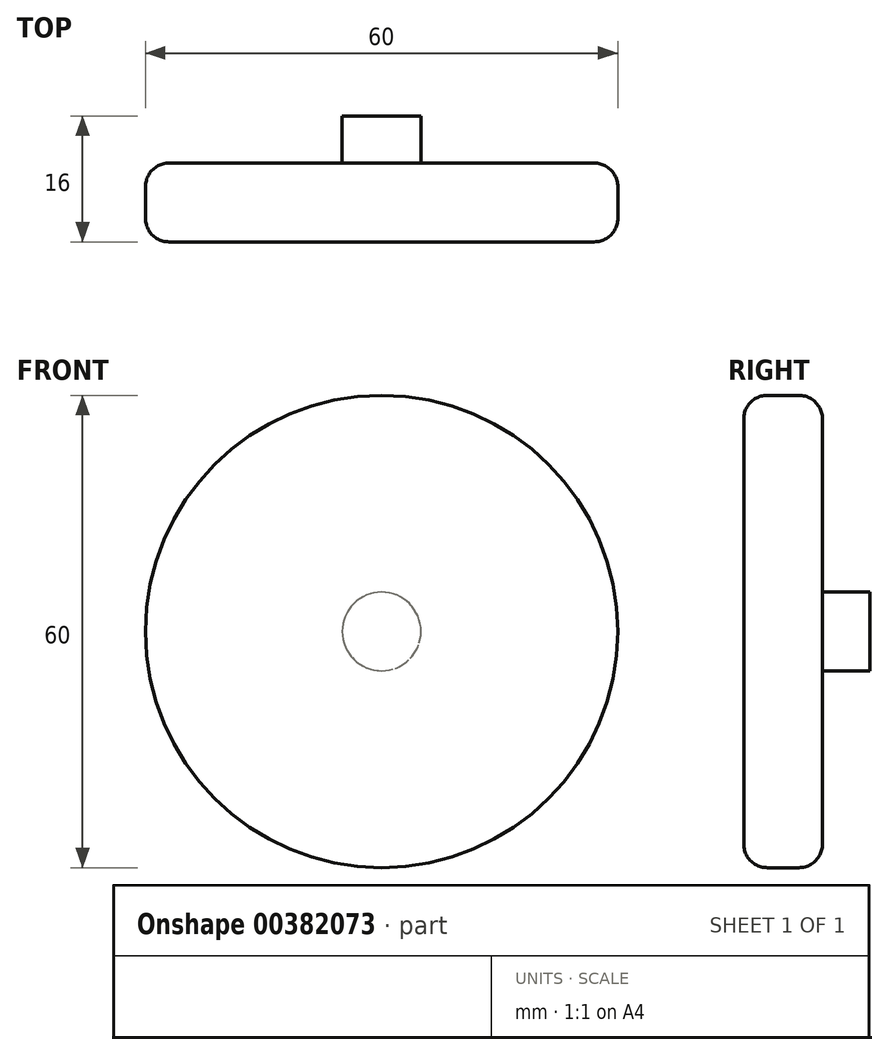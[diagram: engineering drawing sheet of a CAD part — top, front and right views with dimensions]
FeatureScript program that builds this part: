
annotation { "Feature Type Name" : "Feature", "Feature Type Description" : "" }
export const myFeature = defineFeature(function(context is Context, id is Id, definition is map)
    precondition{}
    {
        {
            var Q0;
            Q0=qCreatedBy(makeId("Front.planeOp"),FACE);
            var sketch = newSketch(context, id + "F0", { "sketchPlane" : qUnion([Q0])});
            skCircle(sketch, "E0", {"center": v(0, 0) * mm, "radius": 30 * mm});
            skSolve(sketch);
        }
        {
            var Q0;
            Q0 = qSketchRegion(id + "F0", true);
            extrude(context, id + "F1", {"entities" : qUnion([Q0]), "depth" : 10 * mm});
        }
        {
            var Q0;
            Q0=makeQuery(id+"F1.opExtrude","CAP_EDGE",EDGE,{"disambiguationData":[OSD([sQuery(id+"F0.wireOp",EDGE,"E0")])],"isStart":false});
            var Q1;
            Q1=makeQuery(id+"F1.opExtrude","CAP_EDGE",EDGE,{"disambiguationData":[OSD([sQuery(id+"F0.wireOp",EDGE,"E0")])],"isStart":true});
            fillet(context, id + "F2", {"entities" : qUnion([Q0, Q1]), "radius" : 3 * mm, "tangentPropagation" : true, "allowEdgeOverflow" : false});
        }
        {
            var Q0;
            Q0=makeQuery(id+"F1.opExtrude","CAP_FACE",FACE,{"disambiguationData":[OSD([sQuery(id+"F0.wireOp",EDGE,"E0")])],"isStart":true});
            var sketch = newSketch(context, id + "F3", { "sketchPlane" : qUnion([Q0])});
            skCircle(sketch, "E1", {"center": v(0, 0) * mm, "radius": 5 * mm});
            skSolve(sketch);
        }
        {
            var Q0;
            Q0=makeQuery(id+"F3.imprint","IMPRINT",FACE,{"disambiguationData":[TD([[makeQuery(id+"F3.imprint","IMPRINT",EDGE,{"derivedFrom":sQuery(id+"F3.wireOp",EDGE,"E1")}),1.0]])]});
            extrude(context, id + "F4", {"entities" : qUnion([Q0]), "operationType" : NewBodyOperationType.ADD, "depth" : 6 * mm});
        }
    });
